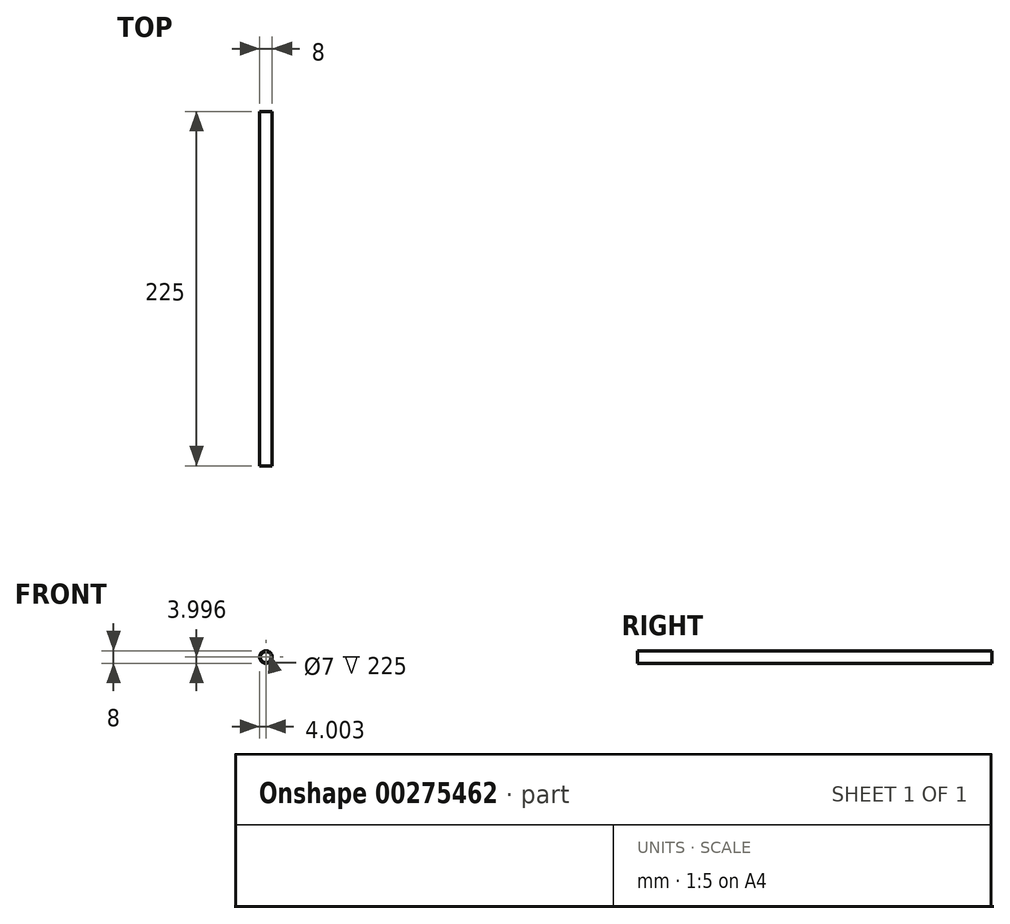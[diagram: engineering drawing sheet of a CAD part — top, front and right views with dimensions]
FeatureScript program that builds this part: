
annotation { "Feature Type Name" : "Feature", "Feature Type Description" : "" }
export const myFeature = defineFeature(function(context is Context, id is Id, definition is map)
    precondition{}
    {
        {
            var Q0;
            Q0=qCreatedBy(makeId("Front.planeOp"),FACE);
            var sketch = newSketch(context, id + "F0", { "sketchPlane" : qUnion([Q0])});
            skCircle(sketch, "E0", {"center": v(-55.57, 33.1) * mm, "radius": 4 * mm});
            skCircle(sketch, "E1", {"center": v(-55.57, 33.1) * mm, "radius": 3.5 * mm});
            skSolve(sketch);
        }
        {
            var Q0;
            Q0=qSketchRegion(id+"F0",true);
            extrude(context, id + "F1", {"entities" : qUnion([Q0]), "depth" : 225 * mm});
        }
    });
